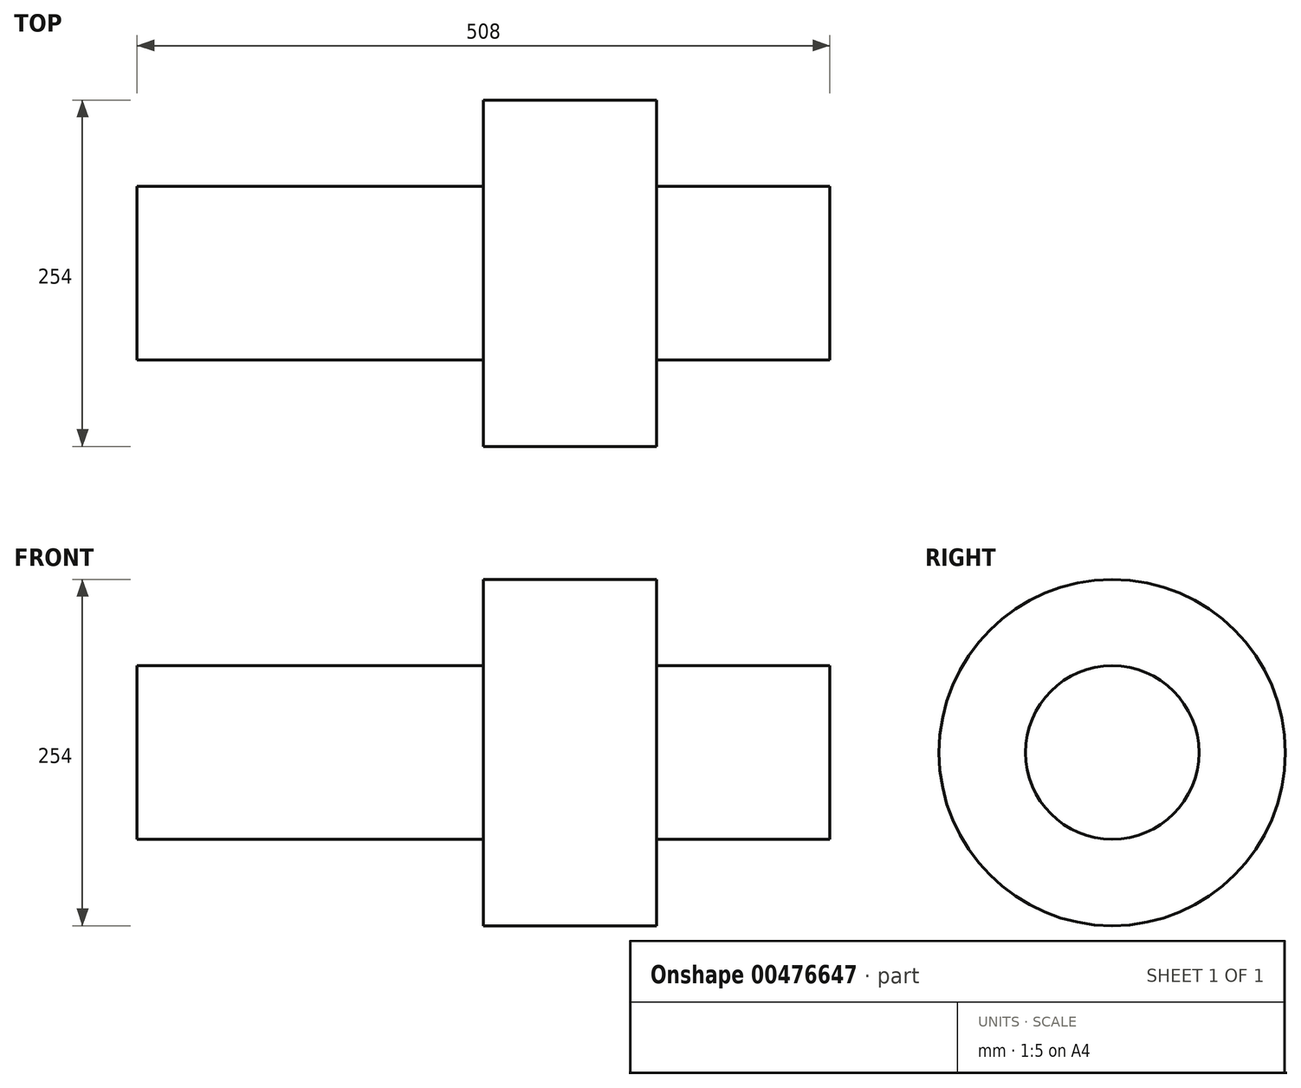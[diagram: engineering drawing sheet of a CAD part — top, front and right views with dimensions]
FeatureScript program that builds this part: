
annotation { "Feature Type Name" : "Feature", "Feature Type Description" : "" }
export const myFeature = defineFeature(function(context is Context, id is Id, definition is map)
    precondition{}
    {
        {
            var Q0;
            Q0=qCreatedBy(makeId("Right.planeOp"),FACE);
            var sketch = newSketch(context, id + "F0", { "sketchPlane" : qUnion([Q0])});
            skCircle(sketch, "E0", {"center": v(0, 0) * mm, "radius": 63.6 * mm});
            skSolve(sketch);
        }
        {
            var Q0;
            Q0=makeQuery(id+"F0.imprint","IMPRINT",FACE,{"disambiguationData":[TD([[makeQuery(id+"F0.imprint","IMPRINT",EDGE,{"derivedFrom":sQuery(id+"F0.wireOp",EDGE,"E0")}),1.0]])]});
            extrude(context, id + "F1", {"entities" : qUnion([Q0]), "depth" : 508 * mm});
        }
        {
            var Q0;
            Q0=makeQuery(id+"F1.opExtrude","CAP_FACE",FACE,{"disambiguationData":[OSD([sQuery(id+"F0.wireOp",EDGE,"E0")])],"isStart":false});
            cPlane(context, id + "F2", {"entities" : qUnion([Q0]), "cplaneType" : CPlaneType.OFFSET, "offset" : 127 * mm, "oppositeDirection" : true, "width" : 152.4 * mm, "height" : 152.4 * mm});
        }
        {
            var Q0;
            Q0=qCreatedBy(id+"F2.planeOp",FACE);
            var sketch = newSketch(context, id + "F3", { "sketchPlane" : qUnion([Q0])});
            skCircle(sketch, "E1", {"center": v(0, 0) * mm, "radius": 127 * mm});
            skSolve(sketch);
        }
        {
            var Q0;
            Q0 = qSketchRegion(id + "F3", true);
            extrude(context, id + "F4", {"entities" : qUnion([Q0]), "operationType" : NewBodyOperationType.ADD, "oppositeDirection" : true, "depth" : 127 * mm});
        }
    });
